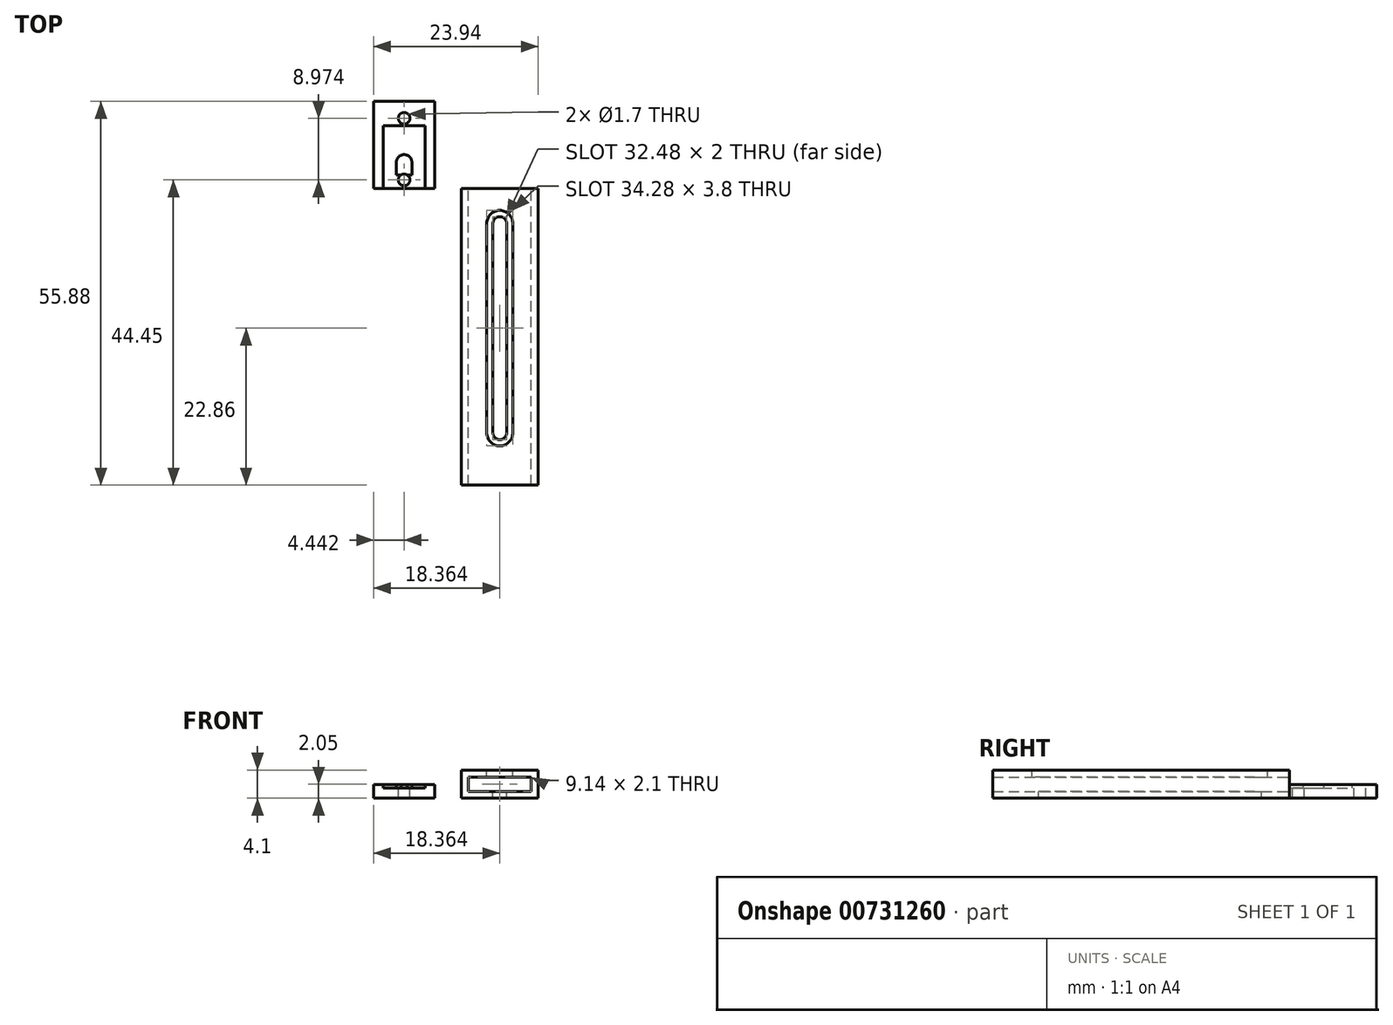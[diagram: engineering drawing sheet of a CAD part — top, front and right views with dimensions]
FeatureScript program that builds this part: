
annotation { "Feature Type Name" : "Feature", "Feature Type Description" : "" }
export const myFeature = defineFeature(function(context is Context, id is Id, definition is map)
    precondition{}
    {
        {
            var Q0;
            Q0=qCreatedBy(makeId("Top.planeOp"),FACE);
            var sketch = newSketch(context, id + "F0", { "sketchPlane" : qUnion([Q0])});
            skLineSegment(sketch, "E0.bottom", {"start": v(0.29, 0) * mm, "end": v(9.18, 0) * mm});
            skLineSegment(sketch, "E0.top", {"start": v(0.29, 12.7) * mm, "end": v(9.18, 12.7) * mm});
            skLineSegment(sketch, "E0.left", {"start": v(0.29, 0) * mm, "end": v(0.29, 12.7) * mm});
            skLineSegment(sketch, "E0.right", {"start": v(9.18, 0) * mm, "end": v(9.18, 12.7) * mm});
            skSolve(sketch);
        }
        {
            var Q0;
            Q0=makeQuery(id+"F0.imprint","IMPRINT",FACE,{"disambiguationData":[TD([[makeQuery(id+"F0.imprint","IMPRINT",EDGE,{"derivedFrom":sQuery(id+"F0.wireOp",EDGE,"E0.bottom")}),1.0]])]});
            extrude(context, id + "F1", {"entities" : qUnion([Q0]), "depth" : 2 * mm, "offsetDistance" : 25.4 * mm});
        }
        {
            var Q0;
            Q0=makeQuery(id+"F1.opExtrude","CAP_FACE",FACE,{"disambiguationData":[OSD([sQuery(id+"F0.wireOp",EDGE,"E0.bottom"),sQuery(id+"F0.wireOp",EDGE,"E0.top"),sQuery(id+"F0.wireOp",EDGE,"E0.left"),sQuery(id+"F0.wireOp",EDGE,"E0.right")])],"isStart":false});
            var sketch = newSketch(context, id + "F2", { "sketchPlane" : qUnion([Q0])});
            skLineSegment(sketch, "E1.bottom", {"start": v(1.68, 0) * mm, "end": v(7.78, 0) * mm});
            skLineSegment(sketch, "E1.top", {"start": v(1.68, 9.14) * mm, "end": v(7.78, 9.14) * mm});
            skLineSegment(sketch, "E1.left", {"start": v(1.68, 0) * mm, "end": v(1.68, 9.14) * mm});
            skLineSegment(sketch, "E1.right", {"start": v(7.78, 0) * mm, "end": v(7.78, 9.14) * mm});
            skLineSegment(sketch, "E2", {"start": v(1.68, 0) * mm, "end": v(0.29, 0) * mm, "construction": true});
            skLineSegment(sketch, "E3", {"start": v(7.78, 0) * mm, "end": v(9.18, 0) * mm, "construction": true});
            skSolve(sketch);
        }
        {
            var Q0;
            Q0=makeQuery(id+"F2.imprint","IMPRINT",FACE,{"disambiguationData":[TD([[makeQuery(id+"F2.imprint","IMPRINT",EDGE,{"derivedFrom":sQuery(id+"F2.wireOp",EDGE,"E1.bottom")}),1.0]])]});
            extrude(context, id + "F3", {"entities" : qUnion([Q0]), "operationType" : NewBodyOperationType.REMOVE, "oppositeDirection" : true, "depth" : 0.5 * mm, "offsetDistance" : 25.4 * mm});
        }
        {
            var Q0;
            Q0=makeQuery(id+"F3.boolean.opBoolean","COPY",FACE,{"derivedFrom":makeQuery(id+"F3.opExtrude","CAP_FACE",FACE,{"disambiguationData":[OSD([sQuery(id+"F2.wireOp",EDGE,"E1.bottom"),sQuery(id+"F2.wireOp",EDGE,"E1.top"),sQuery(id+"F2.wireOp",EDGE,"E1.left"),sQuery(id+"F2.wireOp",EDGE,"E1.right")])],"isStart":false})});
            var sketch = newSketch(context, id + "F4", { "sketchPlane" : qUnion([Q0])});
            skLineSegment(sketch, "E4", {"start": v(3.59, 3.8) * mm, "end": v(3.59, 1.27) * mm});
            skLineSegment(sketch, "E5", {"start": v(3.59, 1.27) * mm, "end": v(5.87, 1.27) * mm, "construction": true});
            skLineSegment(sketch, "E6", {"start": v(5.87, 1.27) * mm, "end": v(5.87, 3.8) * mm});
            skLineSegment(sketch, "E7", {"start": v(5.87, 3.8) * mm, "end": v(3.59, 3.8) * mm, "construction": true});
            skArc(sketch, "E8", {"start": v(5.87, 3.8) * mm, "mid": v(4.73, 4.95) * mm, "end": v(3.59, 3.8) * mm});
            skArc(sketch, "E9", {"start": v(3.59, 1.27) * mm, "mid": v(4.73, 0.13) * mm, "end": v(5.87, 1.27) * mm});
            skLineSegment(sketch, "E10", {"start": v(4.73, 3.8) * mm, "end": v(4.73, 9.14) * mm, "construction": true});
            skSolve(sketch);
        }
        {
            var Q0;
            {var subQ1=sQuery(id+"F4.wireOp",EDGE,"E4");Q0=makeQuery(id+"F4.imprint","IMPRINT",FACE,{"disambiguationData":[TD([[makeQuery(id+"F4.imprint","IMPRINT",EDGE,{"derivedFrom":subQ1}),1.0]])]});}
            extrude(context, id + "F5", {"entities" : qUnion([Q0]), "operationType" : NewBodyOperationType.ADD, "depth" : 0.5 * mm, "offsetDistance" : 25.4 * mm});
        }
        {
            var Q0;
            Q0=makeQuery(id+"F5.opExtrude","CAP_FACE",FACE,{"disambiguationData":[OSD([sQuery(id+"F4.wireOp",EDGE,"E4"),sQuery(id+"F4.wireOp",EDGE,"E6"),sQuery(id+"F4.wireOp",EDGE,"E8"),sQuery(id+"F4.wireOp",EDGE,"E9")])],"isStart":false});
            var sketch = newSketch(context, id + "F6", { "sketchPlane" : qUnion([Q0])});
            skCircle(sketch, "E11", {"center": v(4.73, 1.27) * mm, "radius": 0.85 * mm});
            skCircle(sketch, "E12", {"center": v(4.73, 10.24) * mm, "radius": 0.85 * mm});
            skSolve(sketch);
        }
        {
            var Q0;
            Q0 = qSketchRegion(id + "F6", true);
            extrude(context, id + "F7", {"entities" : qUnion([Q0]), "operationType" : NewBodyOperationType.REMOVE, "oppositeDirection" : true, "depth" : 25.4 * mm, "offsetDistance" : 25.4 * mm});
        }
        {
            var Q0;
            Q0=makeQuery(id+"F5.opExtrude","CAP_FACE",FACE,{"disambiguationData":[OSD([sQuery(id+"F4.wireOp",EDGE,"E4"),sQuery(id+"F4.wireOp",EDGE,"E6"),sQuery(id+"F4.wireOp",EDGE,"E8"),sQuery(id+"F4.wireOp",EDGE,"E9")])],"isStart":false});
            var sketch = newSketch(context, id + "F8", { "sketchPlane" : qUnion([Q0])});
            skLineSegment(sketch, "E13.bottom", {"start": v(2.2, 2) * mm, "end": v(7.27, 2) * mm});
            skLineSegment(sketch, "E13.top", {"start": v(2.2, 0) * mm, "end": v(7.27, 0) * mm});
            skLineSegment(sketch, "E13.left", {"start": v(2.2, 2) * mm, "end": v(2.2, 0) * mm});
            skLineSegment(sketch, "E13.right", {"start": v(7.27, 2) * mm, "end": v(7.27, 0) * mm});
            skSolve(sketch);
        }
        {
            var Q0;
            Q0 = qSketchRegion(id + "F8", true);
            extrude(context, id + "F9", {"entities" : qUnion([Q0]), "operationType" : NewBodyOperationType.REMOVE, "oppositeDirection" : true, "depth" : 0.5 * mm, "offsetDistance" : 25.4 * mm});
        }
        {
            var Q0;
            Q0=qCreatedBy(makeId("Front.planeOp"),FACE);
            var sketch = newSketch(context, id + "F10", { "sketchPlane" : qUnion([Q0])});
            skLineSegment(sketch, "E14.bottom", {"start": v(13.08, 4.1) * mm, "end": v(24.23, 4.1) * mm});
            skLineSegment(sketch, "E14.top", {"start": v(13.08, 0) * mm, "end": v(24.23, 0) * mm});
            skLineSegment(sketch, "E14.left", {"start": v(13.08, 4.1) * mm, "end": v(13.08, 0) * mm});
            skLineSegment(sketch, "E14.right", {"start": v(24.23, 4.1) * mm, "end": v(24.23, 0) * mm});
            skLineSegment(sketch, "E15.bottom", {"start": v(14.08, 3.1) * mm, "end": v(23.23, 3.1) * mm});
            skLineSegment(sketch, "E15.top", {"start": v(14.08, 1) * mm, "end": v(23.23, 1) * mm});
            skLineSegment(sketch, "E15.left", {"start": v(14.08, 3.1) * mm, "end": v(14.08, 1) * mm});
            skLineSegment(sketch, "E15.right", {"start": v(23.23, 3.1) * mm, "end": v(23.23, 1) * mm});
            skLineSegment(sketch, "E16", {"start": v(18.65, 3.1) * mm, "end": v(18.65, 4.1) * mm, "construction": true});
            skLineSegment(sketch, "E17", {"start": v(18.65, 1) * mm, "end": v(18.65, 0) * mm, "construction": true});
            skSolve(sketch);
        }
        {
            var Q0;
            Q0 = qSketchRegion(id + "F10", true);
            extrude(context, id + "F11", {"entities" : qUnion([Q0]), "depth" : 43.18 * mm, "offsetDistance" : 25.4 * mm});
        }
        {
            var Q0;
            Q0=makeQuery(id+"F11.opExtrude","SWEPT_FACE",FACE,{"disambiguationData":[OSD([sQuery(id+"F10.wireOp",EDGE,"E14.bottom")])]});
            var sketch = newSketch(context, id + "F12", { "sketchPlane" : qUnion([Q0])});
            skLineSegment(sketch, "E18.bottom", {"start": v(16.75, -5.08) * mm, "end": v(20.55, -5.08) * mm, "construction": true});
            skLineSegment(sketch, "E18.top", {"start": v(16.75, -35.56) * mm, "end": v(20.55, -35.56) * mm, "construction": true});
            skLineSegment(sketch, "E18.left", {"start": v(16.75, -5.08) * mm, "end": v(16.75, -35.56) * mm});
            skLineSegment(sketch, "E18.right", {"start": v(20.55, -5.08) * mm, "end": v(20.55, -35.56) * mm});
            skArc(sketch, "E19", {"start": v(20.55, -5.08) * mm, "mid": v(18.65, -3.18) * mm, "end": v(16.75, -5.08) * mm});
            skArc(sketch, "E20", {"start": v(16.75, -35.56) * mm, "mid": v(18.65, -37.46) * mm, "end": v(20.55, -35.56) * mm});
            skLineSegment(sketch, "E21", {"start": v(20.55, -35.56) * mm, "end": v(24.23, -35.56) * mm, "construction": true});
            skLineSegment(sketch, "E22", {"start": v(16.75, -35.56) * mm, "end": v(13.08, -35.56) * mm, "construction": true});
            skSolve(sketch);
        }
        {
            var Q0;
            Q0 = qSketchRegion(id + "F12", true);
            extrude(context, id + "F13", {"entities" : qUnion([Q0]), "operationType" : NewBodyOperationType.REMOVE, "oppositeDirection" : true, "depth" : 2.54 * mm, "offsetDistance" : 25.4 * mm});
        }
        {
            var Q0;
            Q0=makeQuery(id+"F11.opExtrude","SWEPT_FACE",FACE,{"disambiguationData":[OSD([sQuery(id+"F10.wireOp",EDGE,"E14.bottom")])]});
            var sketch = newSketch(context, id + "F14", { "sketchPlane" : qUnion([Q0])});
            skLineSegment(sketch, "E23.bottom", {"start": v(17.65, -5.08) * mm, "end": v(19.65, -5.08) * mm, "construction": true});
            skLineSegment(sketch, "E23.top", {"start": v(17.65, -35.56) * mm, "end": v(19.65, -35.56) * mm, "construction": true});
            skLineSegment(sketch, "E23.left", {"start": v(17.65, -5.08) * mm, "end": v(17.65, -35.56) * mm});
            skLineSegment(sketch, "E23.right", {"start": v(19.65, -5.08) * mm, "end": v(19.65, -35.56) * mm});
            skArc(sketch, "E24", {"start": v(19.65, -5.08) * mm, "mid": v(18.65, -4.08) * mm, "end": v(17.65, -5.08) * mm});
            skArc(sketch, "E25", {"start": v(17.65, -35.56) * mm, "mid": v(18.65, -36.56) * mm, "end": v(19.65, -35.56) * mm});
            skSolve(sketch);
        }
        {
            var Q0;
            Q0 = qSketchRegion(id + "F14", true);
            extrude(context, id + "F15", {"entities" : qUnion([Q0]), "operationType" : NewBodyOperationType.REMOVE, "oppositeDirection" : true, "depth" : 25.4 * mm, "offsetDistance" : 25.4 * mm});
        }
    });
